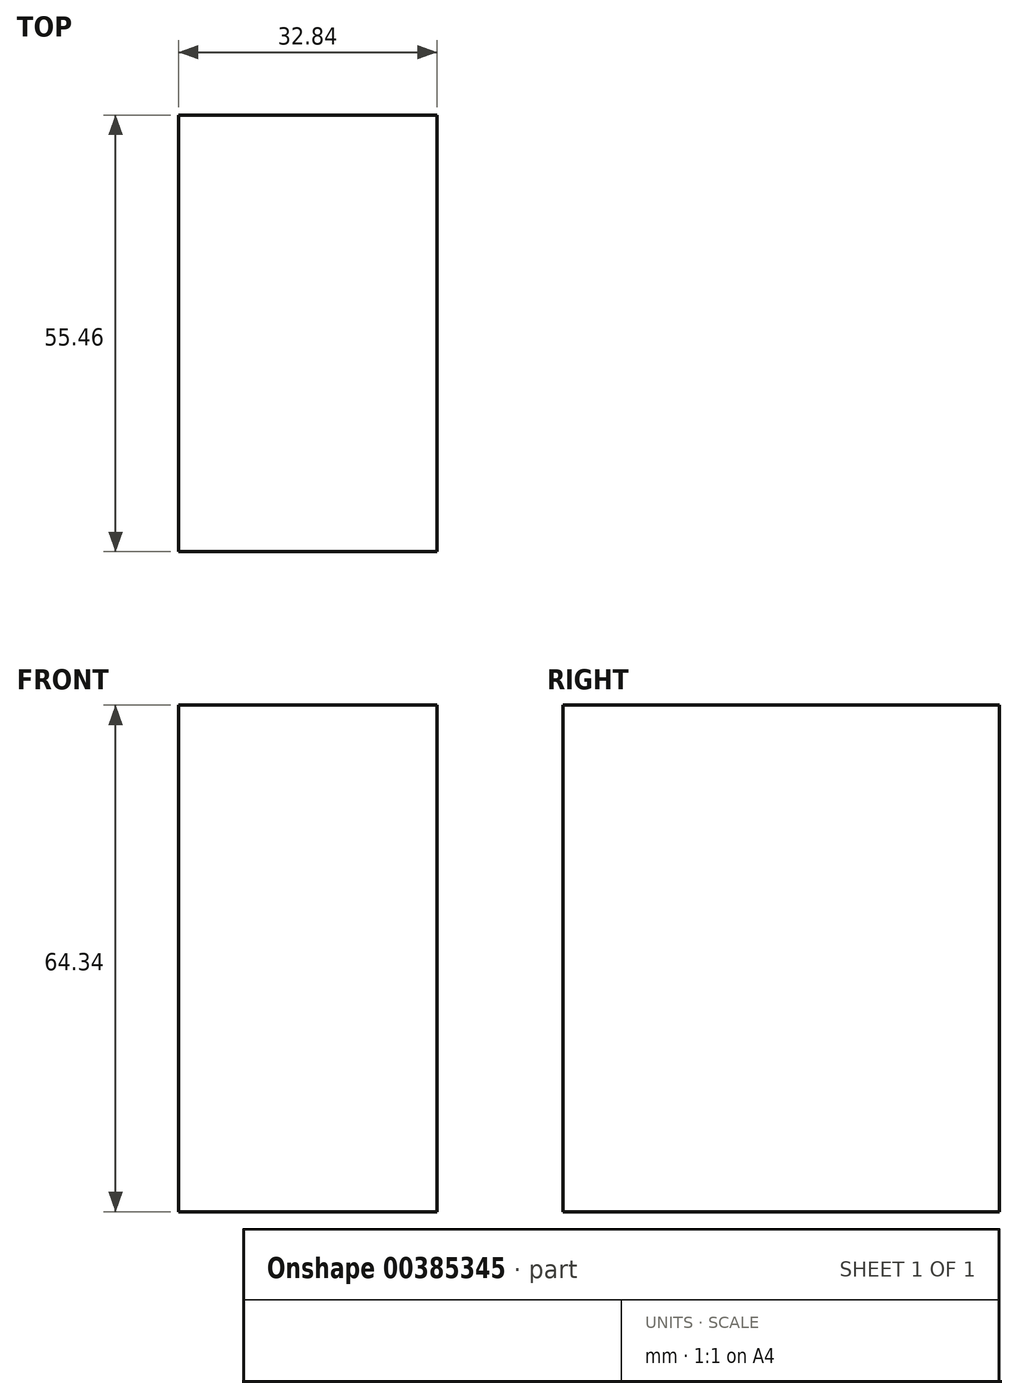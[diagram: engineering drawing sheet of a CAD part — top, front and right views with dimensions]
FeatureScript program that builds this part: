
annotation { "Feature Type Name" : "Feature", "Feature Type Description" : "" }
export const myFeature = defineFeature(function(context is Context, id is Id, definition is map)
    precondition{}
    {
        {
            var Q0;
            Q0=qCreatedBy(makeId("Top.planeOp"),FACE);
            var sketch = newSketch(context, id + "F0", { "sketchPlane" : qUnion([Q0])});
            skLineSegment(sketch, "E0.bottom", {"start": v(-12.3, -9.26) * mm, "end": v(20.55, -9.26) * mm});
            skLineSegment(sketch, "E0.top", {"start": v(-12.3, 46.2) * mm, "end": v(20.55, 46.2) * mm});
            skLineSegment(sketch, "E0.left", {"start": v(-12.3, -9.26) * mm, "end": v(-12.3, 46.2) * mm});
            skLineSegment(sketch, "E0.right", {"start": v(20.55, -9.26) * mm, "end": v(20.55, 46.2) * mm});
            skSolve(sketch);
        }
        {
            var Q0;
            Q0=makeQuery(id+"F0.imprint","IMPRINT",FACE,{"disambiguationData":[TD([[makeQuery(id+"F0.imprint","IMPRINT",EDGE,{"derivedFrom":sQuery(id+"F0.wireOp",EDGE,"E0.bottom")}),1.0]])]});
            extrude(context, id + "F1", {"entities" : qUnion([Q0]), "depth" : 64.34 * mm});
        }
    });
